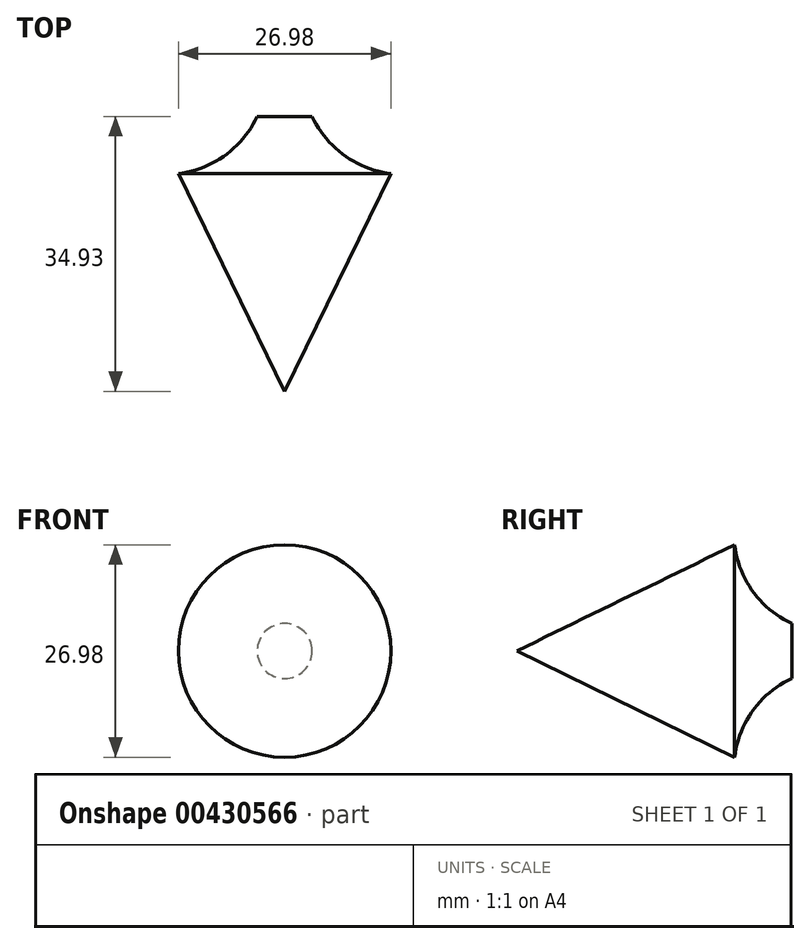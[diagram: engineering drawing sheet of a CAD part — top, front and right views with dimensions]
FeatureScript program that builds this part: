
annotation { "Feature Type Name" : "Feature", "Feature Type Description" : "" }
export const myFeature = defineFeature(function(context is Context, id is Id, definition is map)
    precondition{}
    {
        {
            var Q0;
            Q0=qCreatedBy(makeId("Right.planeOp"),FACE);
            var sketch = newSketch(context, id + "F0", { "sketchPlane" : qUnion([Q0])});
            skLineSegment(sketch, "E0", {"start": v(0, 0) * mm, "end": v(27.67, 13.5) * mm});
            skLineSegment(sketch, "E1", {"start": v(0, 0) * mm, "end": v(34.92, 0) * mm});
            skArc(sketch, "E2", {"start": v(27.67, 13.5) * mm, "mid": v(30, 7.55) * mm, "end": v(34.92, 3.5) * mm});
            skLineSegment(sketch, "E3", {"start": v(34.93, 3.5) * mm, "end": v(34.93, 0) * mm});
            skSolve(sketch);
        }
        {
            var Q0;
            Q0 = qSketchRegion(id + "F0", true);
            var Q1;
            Q1=sQuery(id+"F0.wireOp",EDGE,"E1");
            revolve(context, id + "F1", {"entities" : qUnion([Q0]), "axis" : qUnion([Q1]), "revolveType" : RevolveType.FULL});
        }
    });
